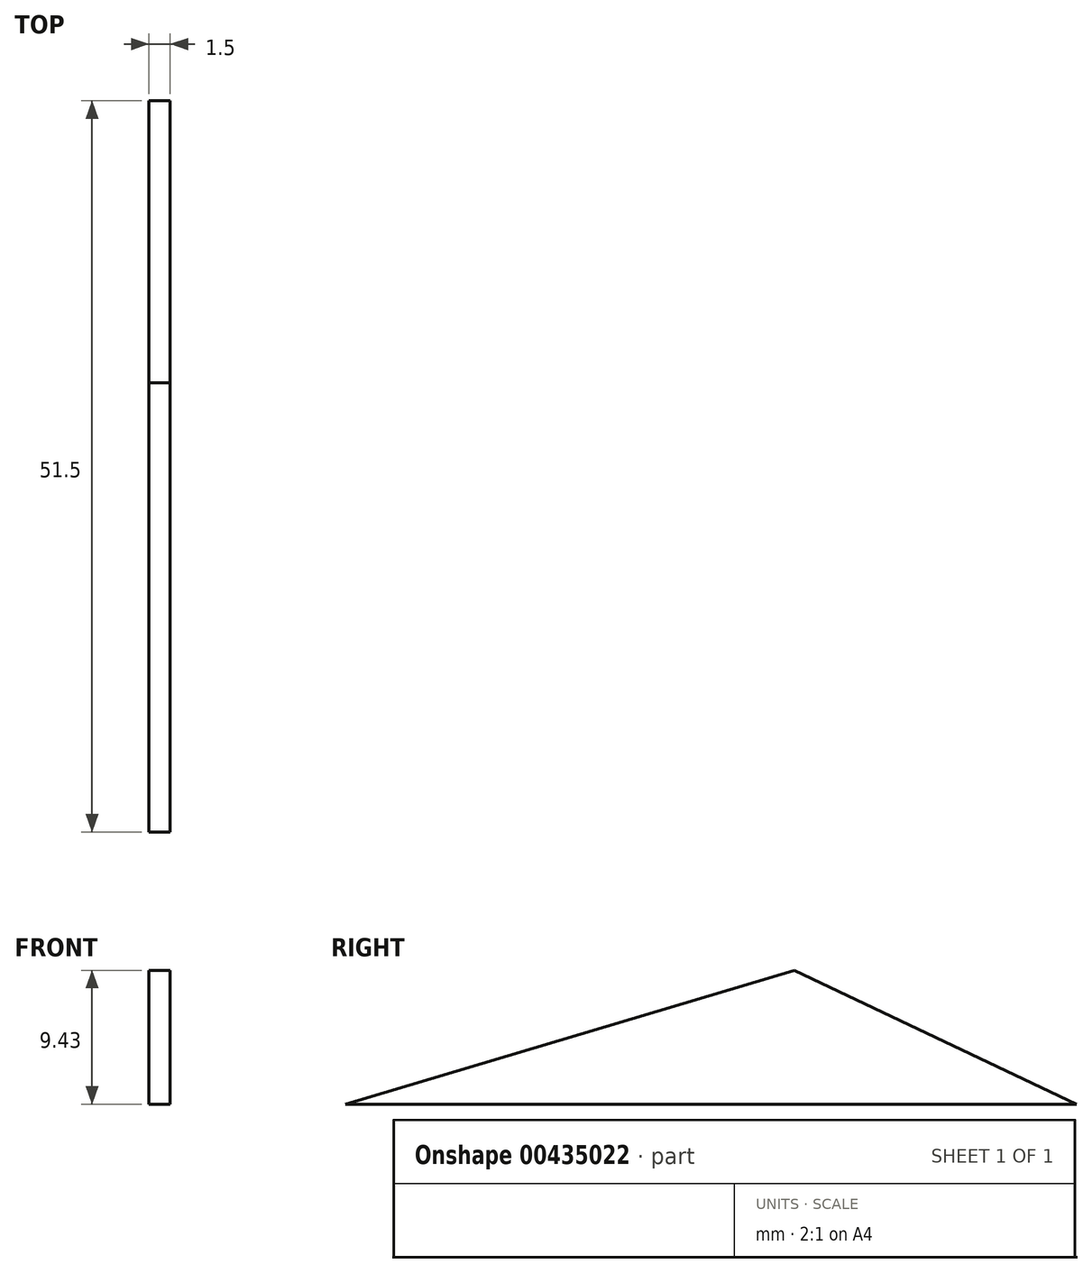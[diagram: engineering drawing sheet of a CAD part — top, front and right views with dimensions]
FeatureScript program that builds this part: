
annotation { "Feature Type Name" : "Feature", "Feature Type Description" : "" }
export const myFeature = defineFeature(function(context is Context, id is Id, definition is map)
    precondition{}
    {
        {
            var Q0;
            Q0=qCreatedBy(makeId("Right.planeOp"),FACE);
            var sketch = newSketch(context, id + "F0", { "sketchPlane" : qUnion([Q0])});
            skLineSegment(sketch, "E0", {"start": v(0, 0) * mm, "end": v(31.62, 9.43) * mm});
            skLineSegment(sketch, "E1", {"start": v(31.62, 9.43) * mm, "end": v(51.5, 0) * mm});
            skLineSegment(sketch, "E2", {"start": v(51.5, 0) * mm, "end": v(0, 0) * mm});
            skSolve(sketch);
        }
        {
            var Q0;
            Q0 = qSketchRegion(id + "F0", true);
            extrude(context, id + "F1", {"entities" : qUnion([Q0]), "depth" : 1.5 * mm});
        }
    });
